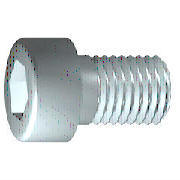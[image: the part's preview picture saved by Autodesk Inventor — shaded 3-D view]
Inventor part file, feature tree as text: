
AUTODESK INVENTOR PART (.ipt)
format: ipt  version: 2013 (Build 170138000, 138)  size: 180,736 bytes
history: native  units: mm (DEFAULTED — no unit token found)
features: sketch x2, extrude x1, plane x1, fillet x1
ambient origin geometry x7: Origin, YZ Plane, XY Plane, X Axis, Y Axis, Z Axis, Center Point
bodies: Solid1 (feature_tree), Body (feature_tree)
feature tree (5):
  extrude  "Slot"  Depth=0.306825mm
  plane  "Work Plane1"
  fillet  "Fillet2"  Radius=3.0mm
  sketch  "Sketch1"  dims[d1=18.0mm d2=0.306825mm d3=3.0mm]
  sketch  "Sketch2"  dims[d4=1.5mm d5=60.0deg d6=3.0mm d7=3.0mm d8=2.886751mm d9=5.5mm d10=90.0deg d11=10.0mm d12=0.0mm d13=18.0mm d14=0.0mm d15=0.306725mm d16=0.306725mm d17=0.3mm d19=0.0mm d26=30.0mm d27=45.0deg d28=0.0mm d29=0.0mm d30=0.1mm]
